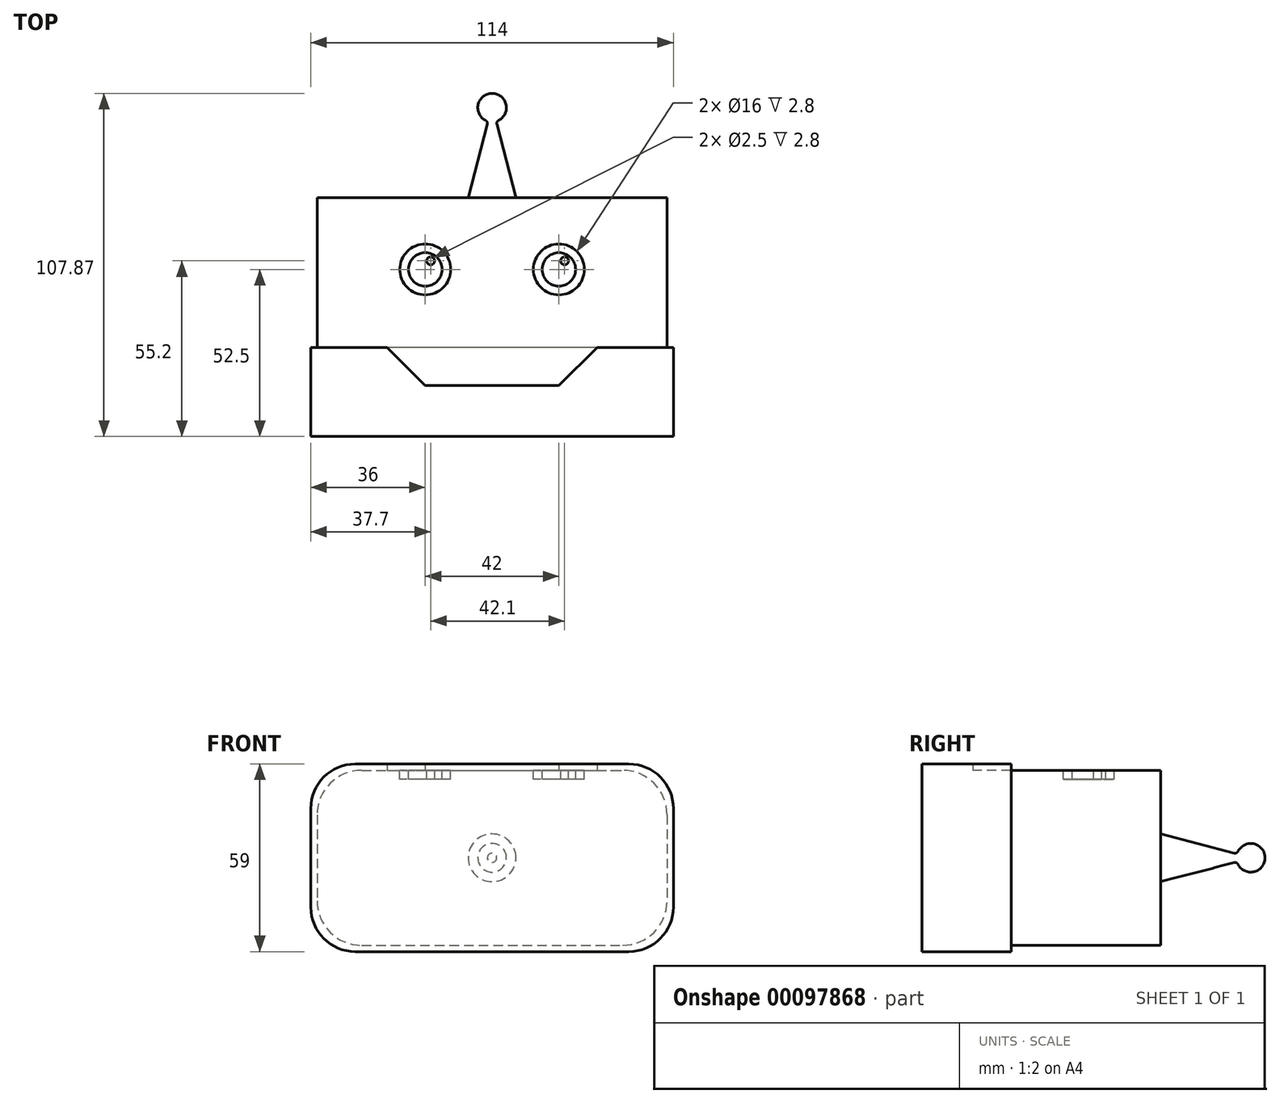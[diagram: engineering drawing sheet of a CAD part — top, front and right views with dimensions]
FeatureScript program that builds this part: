
annotation { "Feature Type Name" : "Feature", "Feature Type Description" : "" }
export const myFeature = defineFeature(function(context is Context, id is Id, definition is map)
    precondition{}
    {
        {
            var Q0;
            Q0=qCreatedBy(makeId("Top.planeOp"),FACE);
            var sketch = newSketch(context, id + "F0", { "sketchPlane" : qUnion([Q0])});
            skLineSegment(sketch, "E0.bottom", {"start": v(-55, 37.5) * mm, "end": v(55, 37.5) * mm});
            skLineSegment(sketch, "E0.top", {"start": v(-55, -37.5) * mm, "end": v(55, -37.5) * mm});
            skLineSegment(sketch, "E0.left", {"start": v(-55, 37.5) * mm, "end": v(-55, -37.5) * mm});
            skLineSegment(sketch, "E0.right", {"start": v(55, 37.5) * mm, "end": v(55, -37.5) * mm});
            skLineSegment(sketch, "E1", {"start": v(0, 37.5) * mm, "end": v(0, -37.5) * mm, "construction": true});
            skLineSegment(sketch, "E2", {"start": v(55, 0) * mm, "end": v(-55, 0) * mm, "construction": true});
            skSolve(sketch);
        }
        {
            var Q0;
            Q0 = qSketchRegion(id + "F0", true);
            extrude(context, id + "F1", {"entities" : qUnion([Q0]), "depth" : 55 * mm});
        }
        {
            var Q0;
            Q0=makeQuery(id+"F1.opExtrude","CAP_FACE",FACE,{"disambiguationData":[OSD([sQuery(id+"F0.wireOp",EDGE,"E0.bottom"),sQuery(id+"F0.wireOp",EDGE,"E0.top"),sQuery(id+"F0.wireOp",EDGE,"E0.left"),sQuery(id+"F0.wireOp",EDGE,"E0.right")])],"isStart":false});
            var sketch = newSketch(context, id + "F2", { "sketchPlane" : qUnion([Q0])});
            skLineSegment(sketch, "E3", {"start": v(-55, -9.5) * mm, "end": v(-33, -9.5) * mm});
            skLineSegment(sketch, "E4", {"start": v(-33, -9.5) * mm, "end": v(-21, -21.54) * mm});
            skLineSegment(sketch, "E5", {"start": v(-21, -21.54) * mm, "end": v(21, -21.54) * mm});
            skLineSegment(sketch, "E6", {"start": v(21, -21.54) * mm, "end": v(33, -9.5) * mm});
            skLineSegment(sketch, "E7", {"start": v(33, -9.5) * mm, "end": v(55, -9.5) * mm});
            skLineSegment(sketch, "E8", {"start": v(0, 37.5) * mm, "end": v(0, -37.5) * mm});
            skLineSegment(sketch, "E9", {"start": v(21, -21.54) * mm, "end": v(0, -21.54) * mm});
            skLineSegment(sketch, "E10", {"start": v(0, -21.54) * mm, "end": v(-21, -21.54) * mm});
            skLineSegment(sketch, "E11", {"start": v(-21, -21.54) * mm, "end": v(0, -21.54) * mm});
            skSolve(sketch);
        }
        {
            var Q0;
            Q0 = qSketchRegion(id + "F2", true);
            var Q1;
            Q1=makeQuery(id+"F2.imprint","IMPRINT",FACE,{"disambiguationData":[TD([[makeQuery(id+"F2.imprint","IMPRINT",EDGE,{"derivedFrom":sQuery(id+"F2.wireOp",EDGE,"E6")}),-1.0]])]});
            var Q2;
            {var subQ4=sQuery(id+"F2.wireOp",EDGE,"E3");Q2=makeQuery(id+"F2.imprint","IMPRINT",FACE,{"disambiguationData":[TD([[makeQuery(id+"F2.imprint","IMPRINT",EDGE,{"derivedFrom":subQ4}),-1.0]])]});}
            extrude(context, id + "F3", {"entities" : qUnion([Q0, Q1, Q2]), "operationType" : NewBodyOperationType.ADD, "depth" : 2 * mm});
        }
        {
            var Q0;
            {var subQ0=sQuery(id+"F0.wireOp",EDGE,"E0.right");Q0=makeQuery(id+"F3.boolean.opBoolean","MERGE",FACE,{"derivedFrom":[makeQuery(id+"F1.opExtrude","SWEPT_FACE",FACE,{"disambiguationData":[OSD([subQ0])]}),makeQuery(id+"F3.opExtrude","SWEPT_FACE",FACE,{"disambiguationData":[OSD([subQ0])]})]});}
            var sketch = newSketch(context, id + "F4", { "sketchPlane" : qUnion([Q0])});
            skLineSegment(sketch, "E12", {"start": v(-9.5, 55) * mm, "end": v(-9.5, 0) * mm});
            skLineSegment(sketch, "E13.0", {"start": v(37.5, 0) * mm, "end": v(-37.5, 0) * mm});
            skLineSegment(sketch, "E13.1", {"start": v(-37.5, 57) * mm, "end": v(-37.5, 0) * mm});
            skLineSegment(sketch, "E13.2", {"start": v(-9.5, 57) * mm, "end": v(-37.5, 57) * mm});
            skPoint(sketch, "E13.3", {"position": v(-9.5, 57) * mm});
            skLineSegment(sketch, "E13.4", {"start": v(-9.5, 57) * mm, "end": v(-9.5, 55) * mm});
            skSolve(sketch);
        }
        {
            var Q0;
            {var subQ2=sQuery(id+"F4.wireOp",EDGE,"E12");Q0=makeQuery(id+"F4.imprint","IMPRINT",FACE,{"disambiguationData":[TD([[makeQuery(id+"F4.imprint","IMPRINT",EDGE,{"derivedFrom":subQ2}),-1.0]])]});}
            extrude(context, id + "F5", {"entities" : qUnion([Q0]), "operationType" : NewBodyOperationType.ADD, "depth" : 2 * mm});
        }
        {
            var Q0;
            Q0=makeQuery(id+"F5.boolean.opBoolean","MERGE",FACE,{"derivedFrom":[makeQuery(id+"F1.opExtrude","CAP_FACE",FACE,{"disambiguationData":[OSD([sQuery(id+"F0.wireOp",EDGE,"E0.bottom"),sQuery(id+"F0.wireOp",EDGE,"E0.top"),sQuery(id+"F0.wireOp",EDGE,"E0.left"),sQuery(id+"F0.wireOp",EDGE,"E0.right")])],"isStart":true}),makeQuery(id+"F5.opExtrude","SWEPT_FACE",FACE,{"disambiguationData":[OSD([sQuery(id+"F4.wireOp",EDGE,"E13.0")])]})]});
            var sketch = newSketch(context, id + "F6", { "sketchPlane" : qUnion([Q0])});
            skLineSegment(sketch, "E14.bottom", {"start": v(57, 9.5) * mm, "end": v(-55, 9.5) * mm});
            skLineSegment(sketch, "E14.top", {"start": v(57, 37.5) * mm, "end": v(-55, 37.5) * mm});
            skLineSegment(sketch, "E14.left", {"start": v(57, 9.5) * mm, "end": v(57, 37.5) * mm});
            skLineSegment(sketch, "E14.right", {"start": v(-55, 9.5) * mm, "end": v(-55, 37.5) * mm});
            skSolve(sketch);
        }
        {
            var Q0;
            Q0 = qSketchRegion(id + "F6", true);
            extrude(context, id + "F7", {"entities" : qUnion([Q0]), "operationType" : NewBodyOperationType.ADD, "depth" : 2 * mm});
        }
        {
            var Q0;
            {var subQ0=sQuery(id+"F0.wireOp",EDGE,"E0.left");Q0=makeQuery(id+"F7.boolean.opBoolean","MERGE",FACE,{"derivedFrom":[makeQuery(id+"F3.boolean.opBoolean","MERGE",FACE,{"derivedFrom":[makeQuery(id+"F1.opExtrude","SWEPT_FACE",FACE,{"disambiguationData":[OSD([subQ0])]}),makeQuery(id+"F3.opExtrude","SWEPT_FACE",FACE,{"disambiguationData":[OSD([subQ0])]})]}),makeQuery(id+"F7.opExtrude","SWEPT_FACE",FACE,{"disambiguationData":[OSD([sQuery(id+"F6.wireOp",EDGE,"E14.right")])]})]});}
            var sketch = newSketch(context, id + "F8", { "sketchPlane" : qUnion([Q0])});
            skLineSegment(sketch, "E15.bottom", {"start": v(9.5, -2) * mm, "end": v(37.5, -2) * mm});
            skLineSegment(sketch, "E15.top", {"start": v(9.5, 57) * mm, "end": v(37.5, 57) * mm});
            skLineSegment(sketch, "E15.left", {"start": v(9.5, -2) * mm, "end": v(9.5, 57) * mm});
            skLineSegment(sketch, "E15.right", {"start": v(37.5, -2) * mm, "end": v(37.5, 57) * mm});
            skSolve(sketch);
        }
        {
            var Q0;
            Q0 = qSketchRegion(id + "F8", true);
            extrude(context, id + "F9", {"entities" : qUnion([Q0]), "operationType" : NewBodyOperationType.ADD, "depth" : 2 * mm});
        }
        {
            var Q0;
            Q0=makeQuery(id+"F9.opExtrude","CAP_EDGE",EDGE,{"disambiguationData":[OSD([sQuery(id+"F8.wireOp",EDGE,"E15.top")])],"isStart":false});
            var Q1;
            Q1=makeQuery(id+"F1.opExtrude","CAP_EDGE",EDGE,{"disambiguationData":[OSD([sQuery(id+"F0.wireOp",EDGE,"E0.left")])],"isStart":false});
            var Q2;
            Q2=makeQuery(id+"F5.opExtrude","CAP_EDGE",EDGE,{"disambiguationData":[OSD([sQuery(id+"F4.wireOp",EDGE,"E13.2")])],"isStart":false});
            var Q3;
            Q3=makeQuery(id+"F1.opExtrude","CAP_EDGE",EDGE,{"disambiguationData":[OSD([sQuery(id+"F0.wireOp",EDGE,"E0.right")])],"isStart":false});
            var Q4;
            Q4=makeQuery(id+"F7.opExtrude","CAP_EDGE",EDGE,{"disambiguationData":[OSD([sQuery(id+"F6.wireOp",EDGE,"E14.left")])],"isStart":false});
            var Q5;
            Q5=makeQuery(id+"F1.opExtrude","CAP_EDGE",EDGE,{"disambiguationData":[OSD([sQuery(id+"F0.wireOp",EDGE,"E0.right")])],"isStart":true});
            var Q6;
            Q6=makeQuery(id+"F1.opExtrude","CAP_EDGE",EDGE,{"disambiguationData":[OSD([sQuery(id+"F0.wireOp",EDGE,"E0.left")])],"isStart":true});
            var Q7;
            Q7=makeQuery(id+"F9.opExtrude","CAP_EDGE",EDGE,{"disambiguationData":[OSD([sQuery(id+"F8.wireOp",EDGE,"E15.bottom")])],"isStart":false});
            fillet(context, id + "F10", {"entities" : qUnion([Q0, Q1, Q2, Q3, Q4, Q5, Q6, Q7]), "radius" : 14 * mm, "tangentPropagation" : true, "allowEdgeOverflow" : false});
        }
        {
            var Q0;
            Q0=makeQuery(id+"F1.opExtrude","CAP_FACE",FACE,{"disambiguationData":[OSD([sQuery(id+"F0.wireOp",EDGE,"E0.bottom"),sQuery(id+"F0.wireOp",EDGE,"E0.top"),sQuery(id+"F0.wireOp",EDGE,"E0.left"),sQuery(id+"F0.wireOp",EDGE,"E0.right")])],"isStart":false});
            var sketch = newSketch(context, id + "F11", { "sketchPlane" : qUnion([Q0])});
            skCircle(sketch, "E16", {"center": v(21, 15) * mm, "radius": 8 * mm});
            skCircle(sketch, "E17", {"center": v(-21, 15) * mm, "radius": 8 * mm});
            skLineSegment(sketch, "E18", {"start": v(41, 15) * mm, "end": v(-41, 15) * mm, "construction": true});
            skPoint(sketch, "E19", {"position": v(0, 15) * mm});
            skCircle(sketch, "E20", {"center": v(-21, 15) * mm, "radius": 5.25 * mm});
            skCircle(sketch, "E21", {"center": v(21, 15) * mm, "radius": 5.25 * mm});
            skCircle(sketch, "E22", {"center": v(-19.3, 17.7) * mm, "radius": 1.25 * mm});
            skCircle(sketch, "E23", {"center": v(22.8, 17.7) * mm, "radius": 1.25 * mm});
            skLineSegment(sketch, "E24", {"start": v(-19.3, 17.7) * mm, "end": v(-19.3, 37.5) * mm});
            skSolve(sketch);
        }
        {
            var Q0;
            Q0=makeQuery(id+"F11.imprint","IMPRINT",FACE,{"disambiguationData":[TD([[makeQuery(id+"F11.imprint","IMPRINT",EDGE,{"derivedFrom":sQuery(id+"F11.wireOp",EDGE,"E17")}),1.0]])]});
            var Q1;
            Q1=makeQuery(id+"F11.imprint","IMPRINT",FACE,{"disambiguationData":[TD([[makeQuery(id+"F11.imprint","IMPRINT",EDGE,{"derivedFrom":sQuery(id+"F11.wireOp",EDGE,"E22")}),1.0]])]});
            var Q2;
            Q2=makeQuery(id+"F11.imprint","IMPRINT",FACE,{"disambiguationData":[TD([[makeQuery(id+"F11.imprint","IMPRINT",EDGE,{"derivedFrom":sQuery(id+"F11.wireOp",EDGE,"E16")}),1.0]])]});
            var Q3;
            Q3=makeQuery(id+"F11.imprint","IMPRINT",FACE,{"disambiguationData":[TD([[makeQuery(id+"F11.imprint","IMPRINT",EDGE,{"derivedFrom":sQuery(id+"F11.wireOp",EDGE,"E23")}),1.0]])]});
            extrude(context, id + "F12", {"entities" : qUnion([Q0, Q1, Q2, Q3]), "operationType" : NewBodyOperationType.REMOVE, "oppositeDirection" : true, "depth" : 2.8 * mm});
        }
        {
            var Q0;
            Q0=qCreatedBy(makeId("Right.planeOp"),FACE);
            var sketch = newSketch(context, id + "F13", { "sketchPlane" : qUnion([Q0])});
            skLineSegment(sketch, "E25", {"start": v(37.5, 27.5) * mm, "end": v(66.5, 27.5) * mm});
            skLineSegment(sketch, "E26", {"start": v(60.7, 29) * mm, "end": v(37.5, 35) * mm});
            skLineSegment(sketch, "E27", {"start": v(37.5, 35) * mm, "end": v(37.5, 27.5) * mm});
            skPoint(sketch, "E28", {"position": v(37.5, 27.5) * mm});
            skArc(sketch, "E29", {"start": v(70.37, 27.5) * mm, "mid": v(66.9, 31.88) * mm, "end": v(61.84, 29.52) * mm});
            skLineSegment(sketch, "E30", {"start": v(70.37, 27.5) * mm, "end": v(61.37, 27.5) * mm});
            skPoint(sketch, "E31.visualSharp", {"position": v(61.55, 28.78) * mm});
            skArc(sketch, "E31.filletArc", {"start": v(60.7, 29) * mm, "mid": v(61.36, 29.06) * mm, "end": v(61.84, 29.52) * mm});
            skSolve(sketch);
        }
        {
            var Q0;
            Q0 = qSketchRegion(id + "F13", true);
            var Q1;
            Q1=sQuery(id+"F13.wireOp",EDGE,"E25");
            revolve(context, id + "F14", {"operationType" : NewBodyOperationType.ADD, "entities" : qUnion([Q0]), "axis" : qUnion([Q1]), "revolveType" : RevolveType.FULL});
        }
    });
